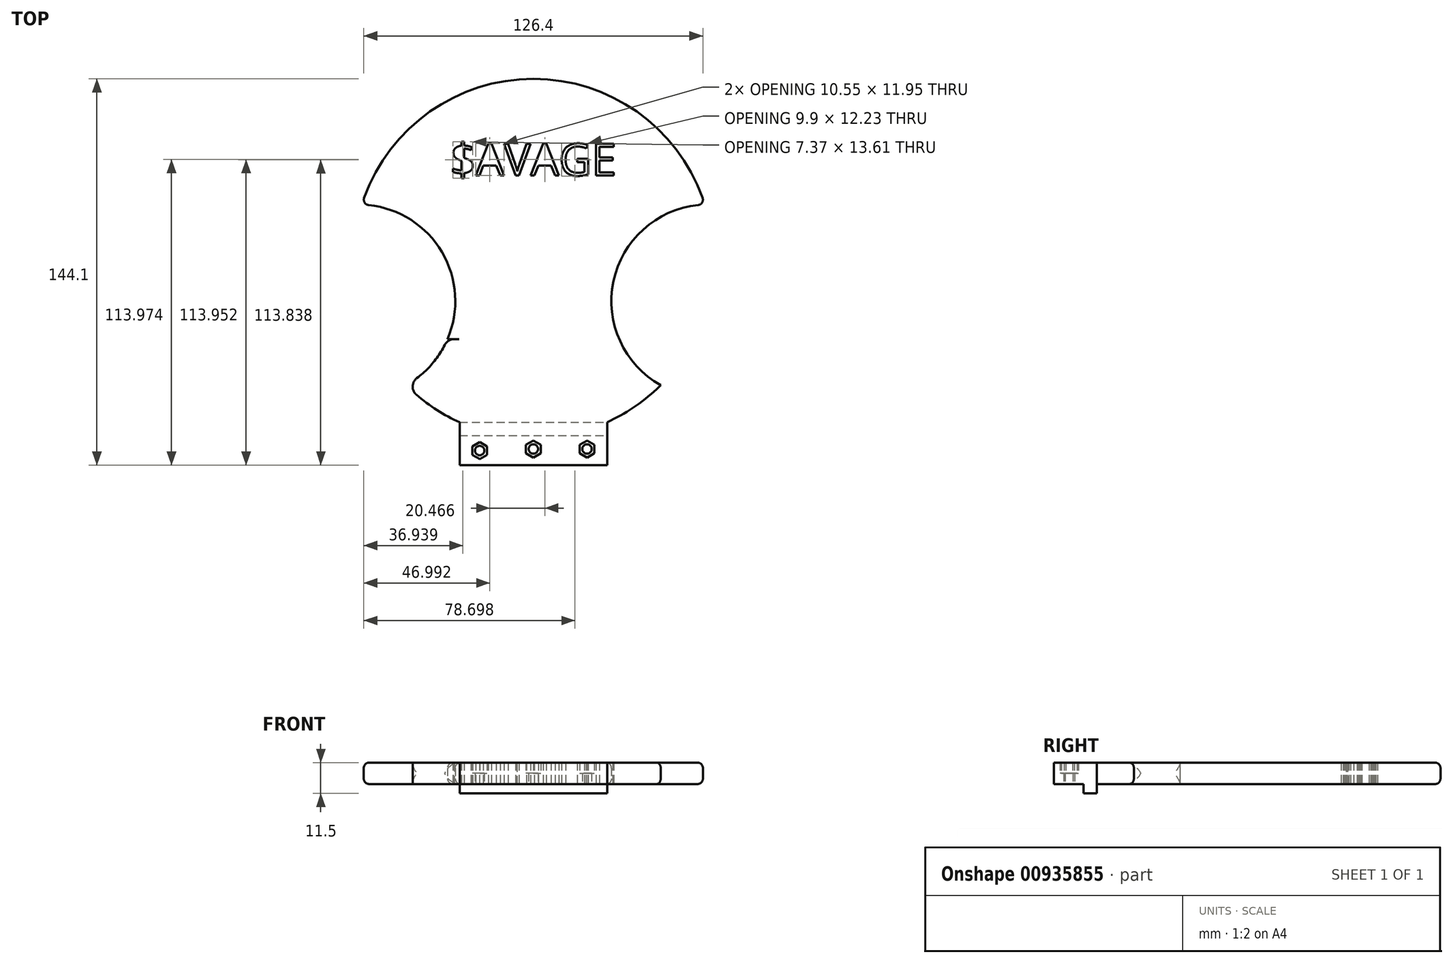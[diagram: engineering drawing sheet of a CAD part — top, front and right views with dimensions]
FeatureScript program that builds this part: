
annotation { "Feature Type Name" : "Feature", "Feature Type Description" : "" }
export const myFeature = defineFeature(function(context is Context, id is Id, definition is map)
    precondition{}
    {
        {
            var Q0;
            Q0=qCreatedBy(makeId("Top.planeOp"),FACE);
            var sketch = newSketch(context, id + "F0", { "sketchPlane" : qUnion([Q0])});
            skLineSegment(sketch, "E0.bottom", {"start": v(-27.5, 8) * mm, "end": v(27.5, 8) * mm});
            skLineSegment(sketch, "E0.top", {"start": v(-27.5, -8) * mm, "end": v(27.5, -8) * mm});
            skLineSegment(sketch, "E0.left", {"start": v(-27.5, 8) * mm, "end": v(-27.5, -8) * mm});
            skLineSegment(sketch, "E0.right", {"start": v(27.5, 8) * mm, "end": v(27.5, -8) * mm});
            skPoint(sketch, "E0.middle", {"position": v(0, 0) * mm});
            skLineSegment(sketch, "E1", {"start": v(-27.5, 3) * mm, "end": v(27.5, 3) * mm});
            skCircle(sketch, "E2.cCircle", {"center": v(0, -2) * mm, "radius": 2.75 * mm, "construction": true});
            skPoint(sketch, "E2.cCircle.centerSnap0", {"position": v(0, -8) * mm});
            skLineSegment(sketch, "E2.0", {"start": v(-2.75, -3.59) * mm, "end": v(-2.75, -0.41) * mm});
            skLineSegment(sketch, "E2.1", {"start": v(-2.75, -0.41) * mm, "end": v(0, 1.18) * mm});
            skLineSegment(sketch, "E2.2", {"start": v(0, 1.18) * mm, "end": v(2.75, -0.41) * mm});
            skLineSegment(sketch, "E2.3", {"start": v(2.75, -0.41) * mm, "end": v(2.75, -3.59) * mm});
            skLineSegment(sketch, "E2.4", {"start": v(2.75, -3.59) * mm, "end": v(0, -5.18) * mm});
            skLineSegment(sketch, "E2.5", {"start": v(0, -5.18) * mm, "end": v(-2.75, -3.59) * mm});
            skPoint(sketch, "E2.0.midPoint", {"position": v(-2.75, -2) * mm});
            skCircle(sketch, "E3", {"center": v(0, -2) * mm, "radius": 1.75 * mm});
            skPoint(sketch, "E4.0.midPoint", {"position": v(-10.58, 0) * mm});
            skCircle(sketch, "E5.cCircle", {"center": v(20, -2) * mm, "radius": 2.75 * mm, "construction": true});
            skLineSegment(sketch, "E5.0", {"start": v(17.25, -0.41) * mm, "end": v(20, 1.18) * mm});
            skLineSegment(sketch, "E5.1", {"start": v(20, 1.18) * mm, "end": v(22.75, -0.41) * mm});
            skLineSegment(sketch, "E5.2", {"start": v(22.75, -0.41) * mm, "end": v(22.75, -3.59) * mm});
            skLineSegment(sketch, "E5.3", {"start": v(22.75, -3.59) * mm, "end": v(20, -5.18) * mm});
            skLineSegment(sketch, "E5.4", {"start": v(20, -5.18) * mm, "end": v(17.25, -3.59) * mm});
            skLineSegment(sketch, "E5.5", {"start": v(17.25, -3.59) * mm, "end": v(17.25, -0.41) * mm});
            skPoint(sketch, "E5.0.midPoint", {"position": v(18.63, 0.38) * mm});
            skCircle(sketch, "E6", {"center": v(20, -2) * mm, "radius": 1.75 * mm});
            skCircle(sketch, "E7.cCircle", {"center": v(-20, -2.57) * mm, "radius": 2.75 * mm, "construction": true});
            skLineSegment(sketch, "E7.0", {"start": v(-17.25, -0.98) * mm, "end": v(-17.25, -4.16) * mm});
            skLineSegment(sketch, "E7.1", {"start": v(-17.25, -4.16) * mm, "end": v(-20, -5.75) * mm});
            skLineSegment(sketch, "E7.2", {"start": v(-20, -5.75) * mm, "end": v(-22.75, -4.16) * mm});
            skLineSegment(sketch, "E7.3", {"start": v(-22.75, -4.16) * mm, "end": v(-22.75, -0.98) * mm});
            skLineSegment(sketch, "E7.4", {"start": v(-22.75, -0.98) * mm, "end": v(-20, 0.6) * mm});
            skLineSegment(sketch, "E7.5", {"start": v(-20, 0.6) * mm, "end": v(-17.25, -0.98) * mm});
            skPoint(sketch, "E7.0.midPoint", {"position": v(-17.25, -2.57) * mm});
            skCircle(sketch, "E8", {"center": v(-20, -2.57) * mm, "radius": 1.75 * mm});
            skArc(sketch, "E9", {"start": v(27.5, 8) * mm, "mid": v(0, 136.1) * mm, "end": v(-27.5, 8) * mm});
            skCircle(sketch, "E10", {"center": v(-65.08, 53.2) * mm, "radius": 36 * mm});
            skText(sketch, "E11", { "text": "$AVAGE", "fontName": "OpenSans-Regular.ttf"});
            skArc(sketch, "E12", {"start": v(55.83, 87.98) * mm, "mid": v(0, 126) * mm, "end": v(-55.83, 87.98) * mm});
            skCircle(sketch, "E13.MirrorC", {"center": v(65.08, 53.2) * mm, "radius": 36 * mm});
            skLineSegment(sketch, "E14", {"start": v(-32, 39) * mm, "end": v(32, 39) * mm});
            skArc(sketch, "E15.0", {"start": v(56.76, 88.35) * mm, "mid": v(0.72, 127) * mm, "end": v(-56.22, 89.67) * mm});
            skArc(sketch, "E16", {"start": v(-29.38, 48.61) * mm, "mid": v(-25.81, 80.25) * mm, "end": v(-56.22, 89.67) * mm});
            skArc(sketch, "E17.MirrorCS", {"start": v(29.38, 48.61) * mm, "mid": v(25.81, 80.25) * mm, "end": v(56.22, 89.67) * mm});
            skArc(sketch, "E18.0", {"start": v(-30.9, 48.56) * mm, "mid": v(-26.67, 79.73) * mm, "end": v(-56.95, 88.26) * mm});
            skArc(sketch, "E19.0", {"start": v(30.9, 48.56) * mm, "mid": v(26.61, 79.65) * mm, "end": v(56.76, 88.35) * mm});
            const initialGuessF0  = {"E11": [-0.03101, 0.1, 1, 0, 0.012]};
            skSetInitialGuess(sketch, initialGuessF0);
            skSolve(sketch);
        }
        {
            var Q0;
            {var subQ0=sQuery(id+"F0.wireOp",EDGE,"E0.bottom");Q0=makeQuery(id+"F0.imprint","IMPRINT",FACE,{"disambiguationData":[TD([[makeQuery(id+"F0.imprint","IMPRINT",EDGE,{"derivedFrom":subQ0}),-1.0]])]});}
            var Q1;
            {var subQ18=sQuery(id+"F0.wireOp",EDGE,"E0.top");Q1=makeQuery(id+"F0.imprint","IMPRINT",FACE,{"disambiguationData":[TD([[makeQuery(id+"F0.imprint","IMPRINT",EDGE,{"derivedFrom":subQ18}),1.0]])]});}
            extrude(context, id + "F1", {"entities" : qUnion([Q0, Q1]), "depth" : 8 * mm, "offsetDistance" : 25 * mm});
        }
        {
            var Q0;
            Q0=makeQuery(id+"F0.imprint","IMPRINT",FACE,{"disambiguationData":[TD([[makeQuery(id+"F0.imprint","IMPRINT",EDGE,{"derivedFrom":sQuery(id+"F0.wireOp",EDGE,"E2.0")}),-1.0]])]});
            var Q1;
            Q1=makeQuery(id+"F0.imprint","IMPRINT",FACE,{"disambiguationData":[TD([[makeQuery(id+"F0.imprint","IMPRINT",EDGE,{"derivedFrom":sQuery(id+"F0.wireOp",EDGE,"E7.0")}),-1.0]])]});
            var Q2;
            Q2=makeQuery(id+"F0.imprint","IMPRINT",FACE,{"disambiguationData":[TD([[makeQuery(id+"F0.imprint","IMPRINT",EDGE,{"derivedFrom":sQuery(id+"F0.wireOp",EDGE,"E5.0")}),-1.0]])]});
            extrude(context, id + "F2", {"entities" : qUnion([Q0, Q1, Q2]), "operationType" : NewBodyOperationType.ADD, "depth" : 4 * mm, "offsetDistance" : 25 * mm});
        }
        {
            var Q0;
            {var subQ0=sQuery(id+"F0.wireOp",EDGE,"E0.bottom");Q0=makeQuery(id+"F0.imprint","IMPRINT",FACE,{"disambiguationData":[TD([[makeQuery(id+"F0.imprint","IMPRINT",EDGE,{"derivedFrom":subQ0}),-1.0]])]});}
            extrude(context, id + "F3", {"entities" : qUnion([Q0]), "operationType" : NewBodyOperationType.ADD, "oppositeDirection" : true, "depth" : 3.5 * mm, "offsetDistance" : 25 * mm});
        }
        {
            var Q0;
            {var subQ1=sQuery(id+"F0.wireOp",EDGE,"E0.bottom");Q0=makeQuery(id+"F0.imprint","IMPRINT",FACE,{"disambiguationData":[TD([[makeQuery(id+"F0.imprint","IMPRINT",EDGE,{"derivedFrom":subQ1}),1.0]])]});}
            extrude(context, id + "F4", {"entities" : qUnion([Q0]), "operationType" : NewBodyOperationType.ADD, "depth" : 8 * mm, "offsetDistance" : 25 * mm});
        }
        {
            var Q0;
            Q0=makeQuery(id+"F4.opExtrude","SWEPT_FACE",FACE,{"disambiguationData":[OSD([sQuery(id+"F0.wireOp",EDGE,"E10")])]});
            var Q1;
            Q1=makeQuery(id+"F4.opExtrude","SWEPT_FACE",FACE,{"disambiguationData":[OSD([sQuery(id+"F0.wireOp",EDGE,"b542f90a-a1cc-4908-bcdd-dd524b4577f80.MirrorC")])]});
            fillet(context, id + "F5", {"entities" : qUnion([Q0, Q1]), "radius" : 4 * mm, "tangentPropagation" : true, "allowEdgeOverflow" : false});
        }
        {
            var Q0;
            {var subQ1=sQuery(id+"F0.wireOp",EDGE,"b542f90a-a1cc-4908-bcdd-dd524b4577f80.MirrorC");var subQ3=sQuery(id+"F0.wireOp",EDGE,"E9");var subQ4=makeQuery(id+"F0.imprint","INTERSECT",VERTEX,{"disambiguationData":[OD(1.0)],"derivedFrom":[subQ3,subQ1]});Q0=makeQuery(id+"F0.imprint","IMPRINT",FACE,{"disambiguationData":[TD([[makeQuery(id+"F0.imprint","IMPRINT",EDGE,{"disambiguationData":[TD([[subQ4,-1.0]])],"derivedFrom":subQ3}),1.0]])]});}
            var Q1;
            {var subQ5=sQuery(id+"F0.wireOp",EDGE,"SljmkWRx-2CkR-U6Iv-HkEV-0N9bRzy9V6qw");Q1=makeQuery(id+"F0.imprint","IMPRINT",FACE,{"disambiguationData":[TD([[makeQuery(id+"F0.imprint","IMPRINT",EDGE,{"derivedFrom":subQ5}),-1.0]])]});}
            var Q2;
            {var subQ0=sQuery(id+"F0.wireOp",EDGE,"21070c6d-8c9e-486b-845a-f9127fd2068e0.MirrorCS");var subQ1=sQuery(id+"F0.wireOp",EDGE,"E10");var subQ2=makeQuery(id+"F0.imprint","INTERSECT",VERTEX,{"disambiguationData":[OD(0.0)],"derivedFrom":[subQ1,subQ0]});Q2=makeQuery(id+"F0.imprint","IMPRINT",FACE,{"disambiguationData":[TD([[makeQuery(id+"F0.imprint","IMPRINT",EDGE,{"disambiguationData":[TD([[subQ2,1.0]])],"derivedFrom":subQ1}),-1.0]])]});}
            var Q3;
            {var subQ0=sQuery(id+"F0.wireOp",EDGE,"YWrEkZsn-ihe4-PdTd-XbTF-X4lioIuSW1vL");var subQ1=sQuery(id+"F0.wireOp",EDGE,"b542f90a-a1cc-4908-bcdd-dd524b4577f80.MirrorC");var subQ2=makeQuery(id+"F0.imprint","INTERSECT",VERTEX,{"disambiguationData":[OD(0.0)],"derivedFrom":[subQ1,subQ0]});Q3=makeQuery(id+"F0.imprint","IMPRINT",FACE,{"disambiguationData":[TD([[makeQuery(id+"F0.imprint","IMPRINT",EDGE,{"disambiguationData":[TD([[subQ2,1.0]])],"derivedFrom":subQ1}),1.0]])]});}
            var Q4;
            {var subQ5=sQuery(id+"F0.wireOp",EDGE,"1154c691-95c2-4d3c-950a-436a19f8762a.0");Q4=makeQuery(id+"F0.imprint","IMPRINT",FACE,{"disambiguationData":[TD([[makeQuery(id+"F0.imprint","IMPRINT",EDGE,{"derivedFrom":subQ5}),1.0]])]});}
            var Q5;
            {var subQ5=sQuery(id+"F0.wireOp",EDGE,"E15.0");Q5=makeQuery(id+"F0.imprint","IMPRINT",FACE,{"disambiguationData":[TD([[makeQuery(id+"F0.imprint","IMPRINT",EDGE,{"derivedFrom":subQ5}),-1.0]])]});}
            var Q6;
            {var subQ0=sQuery(id+"F0.wireOp",EDGE,"E18.0");var subQ1=sQuery(id+"F0.wireOp",EDGE,"E10");var subQ2=makeQuery(id+"F0.imprint","INTERSECT",VERTEX,{"disambiguationData":[OD(0.0)],"derivedFrom":[subQ1,subQ0]});Q6=makeQuery(id+"F0.imprint","IMPRINT",FACE,{"disambiguationData":[TD([[makeQuery(id+"F0.imprint","IMPRINT",EDGE,{"disambiguationData":[TD([[subQ2,1.0]])],"derivedFrom":subQ1}),-1.0]])]});}
            var Q7;
            {var subQ0=sQuery(id+"F0.wireOp",EDGE,"E12");var subQ1=sQuery(id+"F0.wireOp",EDGE,"E10");var subQ2=makeQuery(id+"F0.imprint","INTERSECT",VERTEX,{"derivedFrom":[subQ1,subQ0]});Q7=makeQuery(id+"F0.imprint","IMPRINT",FACE,{"disambiguationData":[TD([[makeQuery(id+"F0.imprint","IMPRINT",EDGE,{"disambiguationData":[TD([[subQ2,1.0]])],"derivedFrom":subQ1}),-1.0]])]});}
            var Q8;
            {var subQ0=sQuery(id+"F0.wireOp",EDGE,"E13.MirrorC");var subQ1=sQuery(id+"F0.wireOp",EDGE,"E12");var subQ2=makeQuery(id+"F0.imprint","INTERSECT",VERTEX,{"derivedFrom":[subQ1,subQ0]});Q8=makeQuery(id+"F0.imprint","IMPRINT",FACE,{"disambiguationData":[TD([[makeQuery(id+"F0.imprint","IMPRINT",EDGE,{"disambiguationData":[TD([[subQ2,-1.0]])],"derivedFrom":subQ1}),1.0]])]});}
            var Q9;
            {var subQ0=sQuery(id+"F0.wireOp",EDGE,"E16");var subQ1=sQuery(id+"F0.wireOp",EDGE,"E10");var subQ2=makeQuery(id+"F0.imprint","INTERSECT",VERTEX,{"derivedFrom":[subQ1,subQ0]});Q9=makeQuery(id+"F0.imprint","IMPRINT",FACE,{"disambiguationData":[TD([[makeQuery(id+"F0.imprint","IMPRINT",EDGE,{"disambiguationData":[TD([[subQ2,-1.0]])],"derivedFrom":subQ1}),-1.0]])]});}
            var Q10;
            {var subQ0=sQuery(id+"F0.wireOp",EDGE,"E19.0");var subQ1=sQuery(id+"F0.wireOp",EDGE,"E12");var subQ2=makeQuery(id+"F0.imprint","INTERSECT",VERTEX,{"derivedFrom":[subQ1,subQ0]});Q10=makeQuery(id+"F0.imprint","IMPRINT",FACE,{"disambiguationData":[TD([[makeQuery(id+"F0.imprint","IMPRINT",EDGE,{"disambiguationData":[TD([[subQ2,-1.0]])],"derivedFrom":subQ1}),1.0]])]});}
            var Q11;
            {var subQ0=sQuery(id+"F0.wireOp",EDGE,"E19.0");var subQ1=sQuery(id+"F0.wireOp",EDGE,"E12");var subQ2=makeQuery(id+"F0.imprint","INTERSECT",VERTEX,{"derivedFrom":[subQ1,subQ0]});Q11=makeQuery(id+"F0.imprint","IMPRINT",FACE,{"disambiguationData":[TD([[makeQuery(id+"F0.imprint","IMPRINT",EDGE,{"disambiguationData":[TD([[subQ2,-1.0]])],"derivedFrom":subQ1}),-1.0]])]});}
            var Q12;
            {var subQ0=sQuery(id+"F0.wireOp",EDGE,"E17.MirrorCS");var subQ1=sQuery(id+"F0.wireOp",EDGE,"E12");var subQ2=makeQuery(id+"F0.imprint","INTERSECT",VERTEX,{"derivedFrom":[subQ1,subQ0]});Q12=makeQuery(id+"F0.imprint","IMPRINT",FACE,{"disambiguationData":[TD([[makeQuery(id+"F0.imprint","IMPRINT",EDGE,{"disambiguationData":[TD([[subQ2,-1.0]])],"derivedFrom":subQ1}),-1.0]])]});}
            extrude(context, id + "F6", {"entities" : qUnion([Q0, Q1, Q2, Q3, Q4, Q5, Q6, Q7, Q8, Q9, Q10, Q11, Q12]), "depth" : 8 * mm, "offsetDistance" : 25 * mm});
        }
        {
            var Q0;
            Q0=makeQuery(id+"F0.imprint","IMPRINT",FACE,{"disambiguationData":[TD([[makeQuery(id+"F0.imprint","IMPRINT",EDGE,{"derivedFrom":sQuery(id+"F0.wireOp",EDGE,"E11.sketch_text.stroke-0")}),1.0]])]});
            var Q1;
            {var subQ0=sQuery(id+"F0.wireOp",EDGE,"E19.0");var subQ1=sQuery(id+"F0.wireOp",EDGE,"E12");var subQ2=makeQuery(id+"F0.imprint","INTERSECT",VERTEX,{"derivedFrom":[subQ1,subQ0]});Q1=makeQuery(id+"F0.imprint","IMPRINT",FACE,{"disambiguationData":[TD([[makeQuery(id+"F0.imprint","IMPRINT",EDGE,{"disambiguationData":[TD([[subQ2,-1.0]])],"derivedFrom":subQ1}),1.0]])]});}
            var Q2;
            {var subQ0=sQuery(id+"F0.wireOp",EDGE,"E16");var subQ1=sQuery(id+"F0.wireOp",EDGE,"E10");var subQ2=makeQuery(id+"F0.imprint","INTERSECT",VERTEX,{"derivedFrom":[subQ1,subQ0]});Q2=makeQuery(id+"F0.imprint","IMPRINT",FACE,{"disambiguationData":[TD([[makeQuery(id+"F0.imprint","IMPRINT",EDGE,{"disambiguationData":[TD([[subQ2,-1.0]])],"derivedFrom":subQ1}),-1.0]])]});}
            var Q3;
            {var subQ0=sQuery(id+"F0.wireOp",EDGE,"E17.MirrorCS");var subQ1=sQuery(id+"F0.wireOp",EDGE,"E12");var subQ2=makeQuery(id+"F0.imprint","INTERSECT",VERTEX,{"derivedFrom":[subQ1,subQ0]});Q3=makeQuery(id+"F0.imprint","IMPRINT",FACE,{"disambiguationData":[TD([[makeQuery(id+"F0.imprint","IMPRINT",EDGE,{"disambiguationData":[TD([[subQ2,-1.0]])],"derivedFrom":subQ1}),-1.0]])]});}
            extrude(context, id + "F7", {"entities" : qUnion([Q0, Q1, Q2, Q3]), "operationType" : NewBodyOperationType.ADD, "depth" : 8 * mm, "offsetDistance" : 25 * mm});
        }
        {
            var Q0;
            Q0=makeQuery(id+"F6.opExtrude","CAP_EDGE",EDGE,{"disambiguationData":[OSD([sQuery(id+"F0.wireOp",EDGE,"E9")])],"isStart":false});
            var Q1;
            Q1=makeQuery(id+"F6.opExtrude","CAP_EDGE",EDGE,{"disambiguationData":[OSD([sQuery(id+"F0.wireOp",EDGE,"E9")])],"isStart":true});
            var Q2;
            Q2=makeQuery(id+"F6.opExtrude","CAP_EDGE",EDGE,{"disambiguationData":[OSD([sQuery(id+"F0.wireOp",EDGE,"E10")])],"isStart":false});
            var Q3;
            Q3=makeQuery(id+"F6.opExtrude","SWEPT_EDGE",EDGE,{"disambiguationData":[OSD([sQuery(id+"F0.wireOp",EDGE,"E9"),sQuery(id+"F0.wireOp",EDGE,"E10")])]});
            var Q4;
            Q4=makeQuery(id+"F6.opExtrude","CAP_EDGE",EDGE,{"disambiguationData":[OSD([sQuery(id+"F0.wireOp",EDGE,"E10")])],"isStart":true});
            var Q5;
            Q5=makeQuery(id+"F6.opExtrude","CAP_EDGE",EDGE,{"disambiguationData":[OSD([sQuery(id+"F0.wireOp",EDGE,"E13.MirrorC")])],"isStart":false});
            var Q6;
            Q6=makeQuery(id+"F6.opExtrude","SWEPT_EDGE",EDGE,{"disambiguationData":[OSD([sQuery(id+"F0.wireOp",EDGE,"E9"),sQuery(id+"F0.wireOp",EDGE,"E13.MirrorC")])]});
            var Q7;
            Q7=makeQuery(id+"F6.opExtrude","CAP_EDGE",EDGE,{"disambiguationData":[OSD([sQuery(id+"F0.wireOp",EDGE,"E13.MirrorC")])],"isStart":true});
            fillet(context, id + "F8", {"entities" : qUnion([Q0, Q1, Q2, Q3, Q4, Q5, Q6, Q7]), "radius" : 2 * mm, "tangentPropagation" : true, "allowEdgeOverflow" : false});
        }
    });
